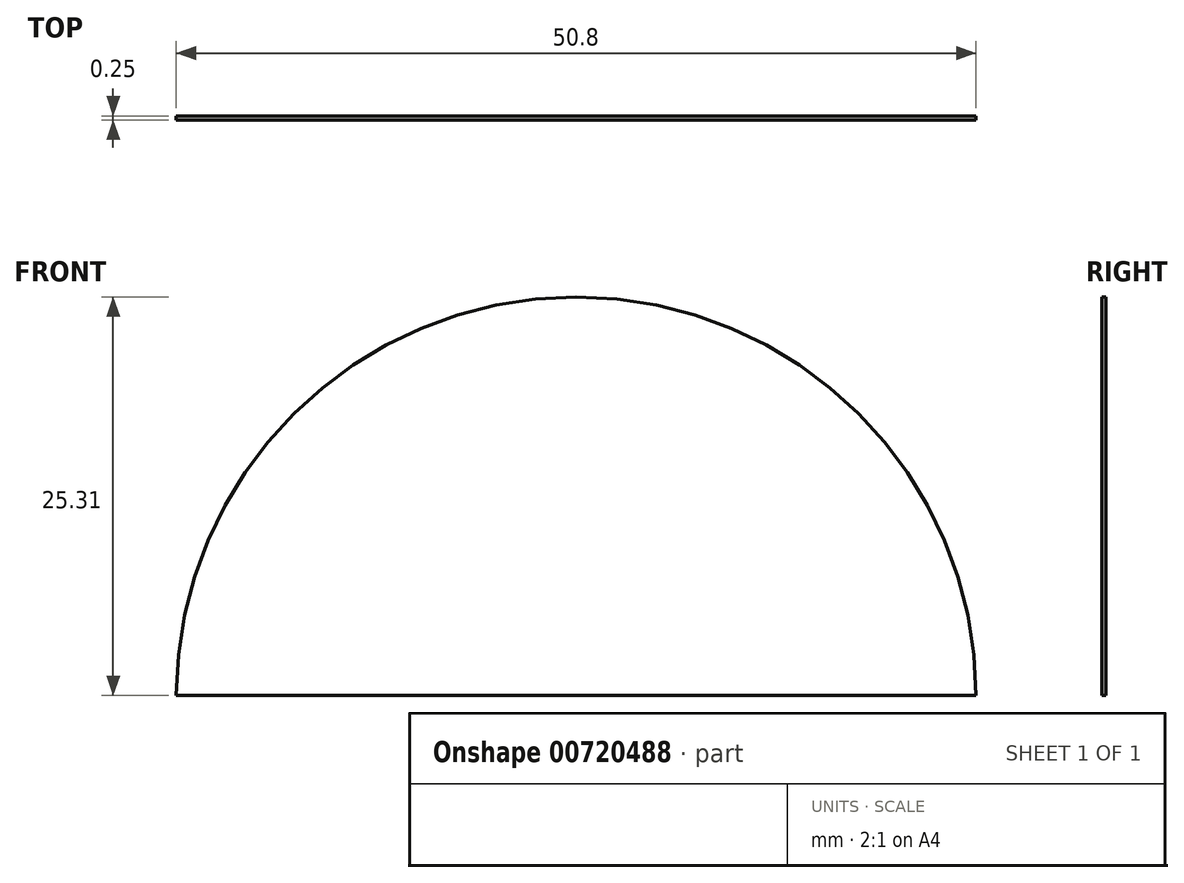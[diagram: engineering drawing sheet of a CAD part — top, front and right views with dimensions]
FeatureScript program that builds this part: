
annotation { "Feature Type Name" : "Feature", "Feature Type Description" : "" }
export const myFeature = defineFeature(function(context is Context, id is Id, definition is map)
    precondition{}
    {
        {
            var Q0;
            Q0=qCreatedBy(makeId("Front.planeOp"),FACE);
            var sketch = newSketch(context, id + "F0", { "sketchPlane" : qUnion([Q0])});
            skArc(sketch, "E0", {"start": v(25.68, 0) * mm, "mid": v(0.28, 25.3) * mm, "end": v(-25.12, 0) * mm});
            skLineSegment(sketch, "E1", {"start": v(-25.12, 0) * mm, "end": v(25.68, 0) * mm});
            skSolve(sketch);
        }
        {
            var Q0;
            Q0=makeQuery(id+"F0.imprint","IMPRINT",FACE,{"disambiguationData":[TD([[makeQuery(id+"F0.imprint","IMPRINT",EDGE,{"derivedFrom":sQuery(id+"F0.wireOp",EDGE,"E0")}),1.0]])]});
            extrude(context, id + "F1", {"entities" : qUnion([Q0]), "depth" : 0.25 * mm, "offsetDistance" : 25.4 * mm});
        }
    });
